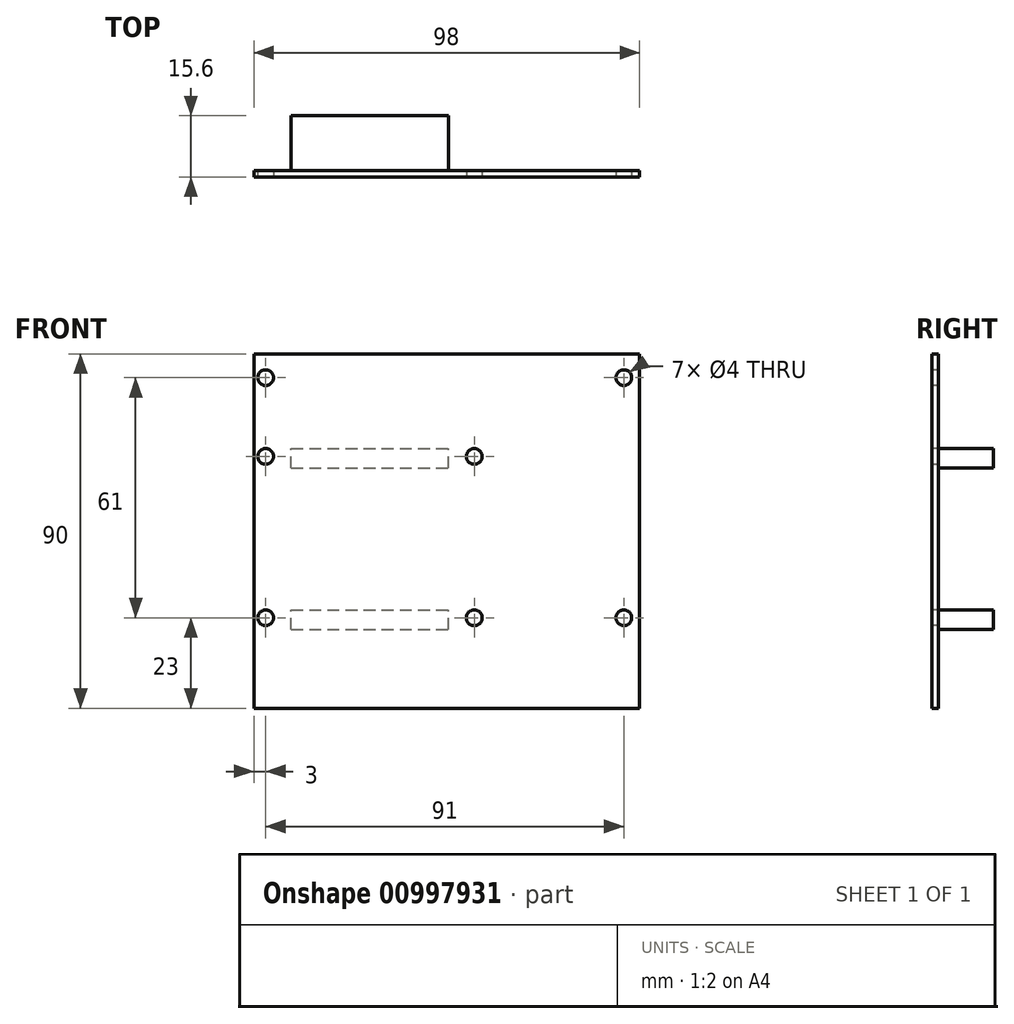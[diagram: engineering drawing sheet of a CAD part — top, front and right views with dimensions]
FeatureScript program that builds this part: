
annotation { "Feature Type Name" : "Feature", "Feature Type Description" : "" }
export const myFeature = defineFeature(function(context is Context, id is Id, definition is map)
    precondition{}
    {
        {
            var Q0;
            Q0=qCreatedBy(makeId("Front.planeOp"),FACE);
            var sketch = newSketch(context, id + "F0", { "sketchPlane" : qUnion([Q0])});
            skLineSegment(sketch, "E0.bottom", {"start": v(49, -45) * mm, "end": v(-49, -45) * mm});
            skLineSegment(sketch, "E0.top", {"start": v(49, 45) * mm, "end": v(-49, 45) * mm});
            skLineSegment(sketch, "E0.left", {"start": v(49, -45) * mm, "end": v(49, 45) * mm});
            skLineSegment(sketch, "E0.right", {"start": v(-49, -45) * mm, "end": v(-49, 45) * mm});
            skPoint(sketch, "E0.middle", {"position": v(0, 0) * mm});
            skSolve(sketch);
        }
        {
            var Q0;
            Q0=makeQuery(id+"F0.imprint","IMPRINT",FACE,{"disambiguationData":[TD([[makeQuery(id+"F0.imprint","IMPRINT",EDGE,{"derivedFrom":sQuery(id+"F0.wireOp",EDGE,"E0.bottom")}),-1.0]])]});
            extrude(context, id + "F1", {"entities" : qUnion([Q0]), "depth" : 1.6 * mm, "offsetDistance" : 25 * mm});
        }
        {
            var Q0;
            Q0=makeQuery(id+"F1.opExtrude","CAP_FACE",FACE,{"disambiguationData":[OSD([sQuery(id+"F0.wireOp",EDGE,"E0.bottom"),sQuery(id+"F0.wireOp",EDGE,"E0.top"),sQuery(id+"F0.wireOp",EDGE,"E0.left"),sQuery(id+"F0.wireOp",EDGE,"E0.right")])],"isStart":false});
            var sketch = newSketch(context, id + "F2", { "sketchPlane" : qUnion([Q0])});
            skCircle(sketch, "E1", {"center": v(-46, 39) * mm, "radius": 2 * mm});
            skCircle(sketch, "E2", {"center": v(45, 39) * mm, "radius": 2 * mm});
            skCircle(sketch, "E3", {"center": v(-46, 19) * mm, "radius": 2 * mm});
            skCircle(sketch, "E4", {"center": v(7, 19) * mm, "radius": 2 * mm});
            skCircle(sketch, "E5", {"center": v(-46, -22) * mm, "radius": 2 * mm});
            skCircle(sketch, "E6", {"center": v(7, -22) * mm, "radius": 2 * mm});
            skCircle(sketch, "E7", {"center": v(45, -22) * mm, "radius": 2 * mm});
            skSolve(sketch);
        }
        {
            var Q0;
            Q0=makeQuery(id+"F2.imprint","IMPRINT",FACE,{"disambiguationData":[TD([[makeQuery(id+"F2.imprint","IMPRINT",EDGE,{"derivedFrom":sQuery(id+"F2.wireOp",EDGE,"E1")}),1.0]])]});
            var Q1;
            Q1=makeQuery(id+"F2.imprint","IMPRINT",FACE,{"disambiguationData":[TD([[makeQuery(id+"F2.imprint","IMPRINT",EDGE,{"derivedFrom":sQuery(id+"F2.wireOp",EDGE,"E3")}),1.0]])]});
            var Q2;
            Q2=makeQuery(id+"F2.imprint","IMPRINT",FACE,{"disambiguationData":[TD([[makeQuery(id+"F2.imprint","IMPRINT",EDGE,{"derivedFrom":sQuery(id+"F2.wireOp",EDGE,"E4")}),1.0]])]});
            var Q3;
            Q3=makeQuery(id+"F2.imprint","IMPRINT",FACE,{"disambiguationData":[TD([[makeQuery(id+"F2.imprint","IMPRINT",EDGE,{"derivedFrom":sQuery(id+"F2.wireOp",EDGE,"E2")}),1.0]])]});
            var Q4;
            Q4=makeQuery(id+"F2.imprint","IMPRINT",FACE,{"disambiguationData":[TD([[makeQuery(id+"F2.imprint","IMPRINT",EDGE,{"derivedFrom":sQuery(id+"F2.wireOp",EDGE,"E5")}),1.0]])]});
            var Q5;
            Q5=makeQuery(id+"F2.imprint","IMPRINT",FACE,{"disambiguationData":[TD([[makeQuery(id+"F2.imprint","IMPRINT",EDGE,{"derivedFrom":sQuery(id+"F2.wireOp",EDGE,"E6")}),1.0]])]});
            var Q6;
            Q6=makeQuery(id+"F2.imprint","IMPRINT",FACE,{"disambiguationData":[TD([[makeQuery(id+"F2.imprint","IMPRINT",EDGE,{"derivedFrom":sQuery(id+"F2.wireOp",EDGE,"E7")}),1.0]])]});
            extrude(context, id + "F3", {"entities" : qUnion([Q0, Q1, Q2, Q3, Q4, Q5, Q6]), "operationType" : NewBodyOperationType.REMOVE, "oppositeDirection" : true, "depth" : 25 * mm, "offsetDistance" : 25 * mm});
        }
        {
            var Q0;
            Q0=makeQuery(id+"F1.opExtrude","CAP_FACE",FACE,{"disambiguationData":[OSD([sQuery(id+"F0.wireOp",EDGE,"E0.bottom"),sQuery(id+"F0.wireOp",EDGE,"E0.top"),sQuery(id+"F0.wireOp",EDGE,"E0.left"),sQuery(id+"F0.wireOp",EDGE,"E0.right")])],"isStart":true});
            var sketch = newSketch(context, id + "F4", { "sketchPlane" : qUnion([Q0])});
            skLineSegment(sketch, "E8.bottom", {"start": v(39.5, 16) * mm, "end": v(-0.5, 16) * mm});
            skLineSegment(sketch, "E8.top", {"start": v(39.5, 21) * mm, "end": v(-0.5, 21) * mm});
            skLineSegment(sketch, "E8.left", {"start": v(39.5, 16) * mm, "end": v(39.5, 21) * mm});
            skLineSegment(sketch, "E8.right", {"start": v(-0.5, 16) * mm, "end": v(-0.5, 21) * mm});
            skPoint(sketch, "E8.middle", {"position": v(19.5, 18.5) * mm});
            skLineSegment(sketch, "E9.bottom", {"start": v(39.5, -25) * mm, "end": v(-0.5, -25) * mm});
            skLineSegment(sketch, "E9.top", {"start": v(39.5, -20) * mm, "end": v(-0.5, -20) * mm});
            skLineSegment(sketch, "E9.left", {"start": v(39.5, -25) * mm, "end": v(39.5, -20) * mm});
            skLineSegment(sketch, "E9.right", {"start": v(-0.5, -25) * mm, "end": v(-0.5, -20) * mm});
            skPoint(sketch, "E9.middle", {"position": v(19.5, -22.5) * mm});
            skSolve(sketch);
        }
        {
            var Q0;
            Q0 = qSketchRegion(id + "F4", true);
            extrude(context, id + "F5", {"entities" : qUnion([Q0]), "operationType" : NewBodyOperationType.ADD, "depth" : 14 * mm, "offsetDistance" : 25 * mm});
        }
    });
